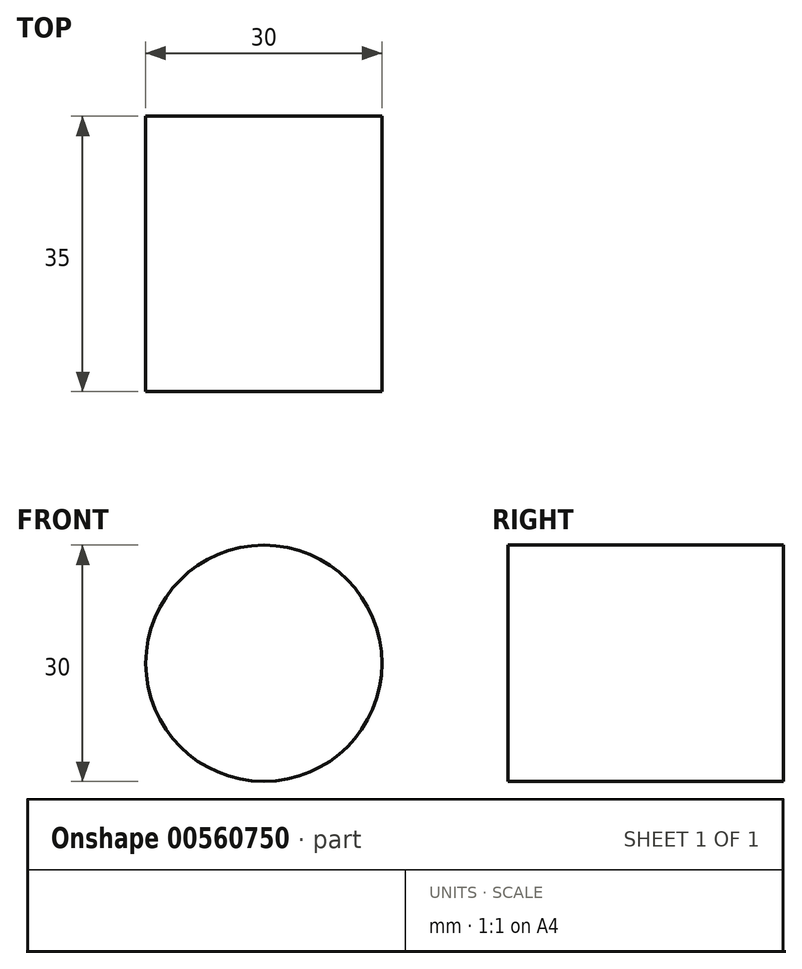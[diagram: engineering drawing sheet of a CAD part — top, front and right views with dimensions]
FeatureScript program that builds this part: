
annotation { "Feature Type Name" : "Feature", "Feature Type Description" : "" }
export const myFeature = defineFeature(function(context is Context, id is Id, definition is map)
    precondition{}
    {
        {
            var Q0;
            Q0=qCreatedBy(makeId("Front.planeOp"),FACE);
            var sketch = newSketch(context, id + "F0", { "sketchPlane" : qUnion([Q0])});
            skCircle(sketch, "E0", {"center": v(0, 0) * mm, "radius": 15 * mm});
            skSolve(sketch);
        }
        {
            var Q0;
            Q0 = qSketchRegion(id + "F0", true);
            var Q1;
            Q1=makeQuery(id+"F0.imprint","IMPRINT",FACE,{"disambiguationData":[TD([[makeQuery(id+"F0.imprint","IMPRINT",EDGE,{"derivedFrom":sQuery(id+"F0.wireOp",EDGE,"E0")}),1.0]])]});
            extrude(context, id + "F1", {"entities" : qUnion([Q0, Q1]), "depth" : 35 * mm, "offsetDistance" : 25 * mm});
        }
    });
